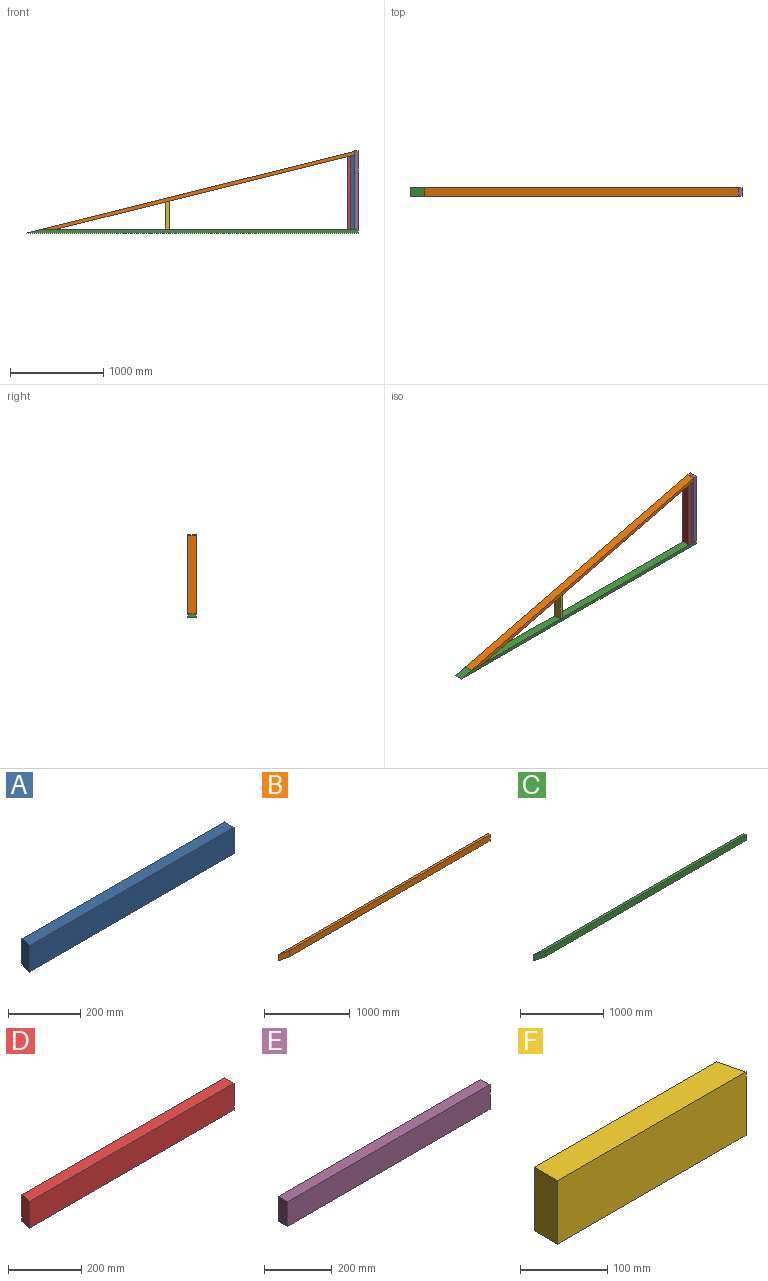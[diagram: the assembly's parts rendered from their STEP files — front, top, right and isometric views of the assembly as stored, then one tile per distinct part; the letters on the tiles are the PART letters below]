
ASSEMBLY  parts=6 mates=15
PART A: 6 faces, bbox 799.8x38.1x88.9 mm
  f0: plane 799.8x38.1mm, normal (0,0,1), area 30291.6mm2, adj f1,f2,f4,f5
  f1: plane 799.8x88.9mm, normal (0,-1,0), area 71102.6mm2, adj f0,f3,f4,f5
  f2: plane 790.31x88.9mm, normal (0,1,0), area 70258.1mm2, adj f0,f3,f4,f5
  f3: plane 799.8x38.1mm, normal (0,0,-1), area 30291.6mm2, adj f1,f2,f4,f5
  f4: plane 88.9x38.1mm, normal (1,0,0), area 3387.1mm2, adj f0,f1,f2,f3
  f5: plane 88.9x38.1mm, normal (-0.97,0.24,0), area 3490.8mm2, adj f0,f1,f2,f3
PART B: 6 faces, bbox 3468.4x38.1x88.9 mm
  f0: plane 3468.35x38.1mm, normal (0,0,1), area 129052.3mm2, adj f1,f3,f4,f5
  f1: plane 3306.04x88.9mm, normal (0,-1,0), area 293907.2mm2, adj f0,f2,f4,f5
  f2: plane 3468.35x38.1mm, normal (0,0,-1), area 129052.3mm2, adj f1,f3,f4,f5
  f3: plane 3468.35x88.9mm, normal (0,1,0), area 308336.6mm2, adj f0,f2,f4,f5
  f4: plane 88.9x38.1mm, normal (0.97,-0.24,0), area 3490.8mm2, adj f0,f1,f2,f3
  f5: plane 152.81x88.9mm, normal (-0.24,-0.97,0), area 14000.8mm2, adj f0,f1,f2,f3
PART C: 6 faces, bbox 3555.5x38.1x88.9 mm
  f0: plane 3402.71x88.9mm, normal (0,-1,0), area 302500.7mm2, adj f2,f3,f4,f5
  f1: plane 3555.52x88.9mm, normal (0,1,0), area 316085.6mm2, adj f2,f3,f4,f5
  f2: plane 3555.52x38.1mm, normal (0,0,1), area 132554.2mm2, adj f0,f1,f4,f5
  f3: plane 3555.52x38.1mm, normal (0,0,-1), area 132554.2mm2, adj f0,f1,f4,f5
  f4: plane 88.9x38.1mm, normal (1,0,0), area 3387.1mm2, adj f0,f1,f2,f3
  f5: plane 152.81x88.9mm, normal (-0.24,-0.97,0), area 14000.8mm2, adj f0,f1,f2,f3
PART D: 6 faces, bbox 790.3x38.1x88.9 mm
  f0: plane 790.31x38.1mm, normal (0,0,1), area 29929.7mm2, adj f1,f2,f4,f5
  f1: plane 790.31x88.9mm, normal (0,-1,0), area 70258.1mm2, adj f0,f3,f4,f5
  f2: plane 780.81x88.9mm, normal (0,1,0), area 69413.6mm2, adj f0,f3,f4,f5
  f3: plane 790.31x38.1mm, normal (0,0,-1), area 29929.7mm2, adj f1,f2,f4,f5
  f4: plane 88.9x38.1mm, normal (1,0,0), area 3387.1mm2, adj f0,f1,f2,f3
  f5: plane 88.9x38.1mm, normal (-0.97,0.24,0), area 3490.8mm2, adj f0,f1,f2,f3
PART E: 6 faces, bbox 844.5x38.1x88.9 mm
  f0: plane 844.52x38.1mm, normal (0,0,1), area 32176.4mm2, adj f1,f3,f4,f5
  f1: plane 844.52x88.9mm, normal (0,-1,0), area 75078.2mm2, adj f0,f2,f4,f5
  f2: plane 844.52x38.1mm, normal (0,0,-1), area 32176.4mm2, adj f1,f3,f4,f5
  f3: plane 844.52x88.9mm, normal (0,1,0), area 75078.2mm2, adj f0,f2,f4,f5
  f4: plane 88.9x38.1mm, normal (1,0,0), area 3387.1mm2, adj f0,f1,f2,f3
  f5: plane 88.9x38.1mm, normal (-1,0,0), area 3387.1mm2, adj f0,f1,f2,f3
PART F: 6 faces, bbox 304.8x38.1x88.9 mm
  f0: plane 304.8x38.1mm, normal (0,0,1), area 11431.9mm2, adj f2,f3,f4,f5
  f1: plane 304.8x38.1mm, normal (0,0,-1), area 11431.9mm2, adj f2,f3,f4,f5
  f2: plane 304.8x88.9mm, normal (0,-1,0), area 27096.7mm2, adj f0,f1,f4,f5
  f3: plane 295.3x88.9mm, normal (0,1,0), area 26252.2mm2, adj f0,f1,f4,f5
  f4: plane 88.9x38.1mm, normal (-1,0,0), area 3387.1mm2, adj f0,f1,f2,f3
  f5: plane 88.9x38.1mm, normal (0.97,0.24,0), area 3490.8mm2, adj f0,f1,f2,f3
PLACE A rot(axis=(-0.58,0.58,0.58),120deg) t=(-57.15,-44.45,2108.2)mm
PLACE B rot(axis=(0.99,-0.12,0.12),90.9deg) t=(-1353.24,-44.45,491.54)mm
PLACE C rot(axis=(-1,0,0),90deg) t=(-1822.45,-44.45,-19.05)mm
PLACE D rot(axis=(-0.58,0.58,0.58),120deg) t=(-95.25,-44.45,488.19)mm
PLACE E rot(axis=(-0.58,-0.58,-0.58),120deg) t=(-19.05,-44.45,422.26)mm
PLACE F rot(axis=(0.58,-0.58,0.58),120deg) t=(-2042.5,-44.45,152.4)mm
MATE planar B.f0 <-> C.f3  axis (0,-1,0) through (-1681.71,-88.9,409.8)mm
MATE planar C.f0 <-> E.f5  axis (0,0,1) through (0,0,0)mm
MATE planar E.f3 <-> C.f4  axis (1,0,0) through (0,-44.45,422.26)mm
MATE planar D.f3 <-> C.f3  axis (0,-1,0) through (-95.21,-88.9,392.78)mm
MATE planar F.f4 <-> C.f0  axis (0,0,-1) through (-2042.5,-44.45,0)mm
MATE planar A.f4 <-> C.f0  axis (0,0,-1) through (-57.15,-44.45,0)mm
MATE planar A.f1 <-> E.f1  axis (1,0,0) through (-38.1,-44.45,399.9)mm
MATE planar D.f4 <-> C.f0  axis (0,0,-1) through (-95.25,-44.45,0)mm
MATE planar E.f2 <-> C.f3  axis (0,-1,0) through (-19.05,-88.9,422.26)mm
MATE planar A.f3 <-> C.f3  axis (0,-1,0) through (-57.11,-88.9,397.53)mm
MATE planar D.f1 <-> A.f2  axis (1,0,0) through (-76.2,-44.45,395.15)mm
MATE planar B.f5 <-> C.f0  axis (0,0,-1) through (-3324.68,-44.45,0)mm
MATE planar F.f0 <-> C.f3  axis (0,-1,0) through (-2042.4,-88.9,150.04)mm
MATE planar B.f4 <-> E.f1  axis (1,0,0) through (-38.1,-44.45,819.44)mm
MATE planar F.f5 <-> B.f1  axis (-0.24,0,0.97) through (-2042.5,-44.45,300.05)mm
